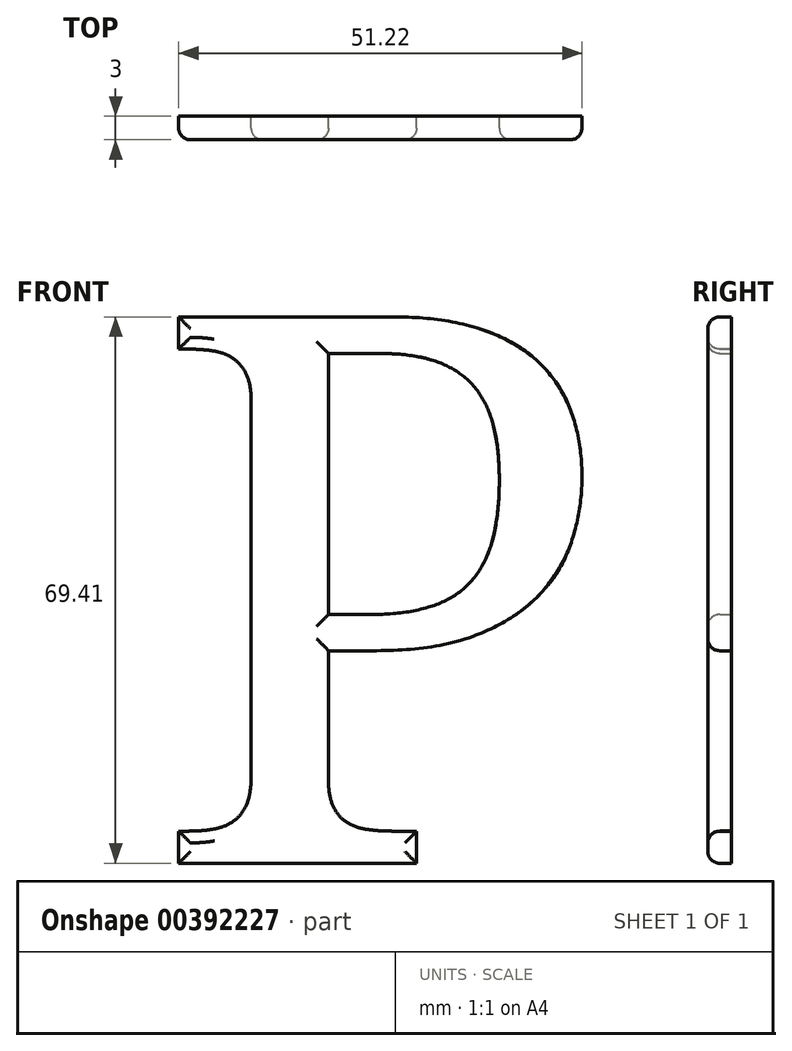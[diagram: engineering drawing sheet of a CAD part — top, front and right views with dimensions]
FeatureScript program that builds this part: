
annotation { "Feature Type Name" : "Feature", "Feature Type Description" : "" }
export const myFeature = defineFeature(function(context is Context, id is Id, definition is map)
    precondition{}
    {
        {
            var Q0;
            Q0=qCreatedBy(makeId("Front.planeOp"),FACE);
            var sketch = newSketch(context, id + "F0", { "sketchPlane" : qUnion([Q0])});
            skText(sketch, "E0", { "text": "P", "fontName": "NotoSerif-Regular.ttf"});
            const initialGuessF0  = {"E0": [0, 0, 1, 0, 0.07]};
            skSetInitialGuess(sketch, initialGuessF0);
            skSolve(sketch);
        }
        {
            var Q0;
            Q0 = qSketchRegion(id + "F0", true);
            extrude(context, id + "F1", {"entities" : qUnion([Q0]), "depth" : 3 * mm});
        }
        {
            var Q0;
            Q0=makeQuery(id+"F1.opExtrude","CAP_FACE",FACE,{"disambiguationData":[OSD([sQuery(id+"F0.wireOp",EDGE,"E0.sketch_text.stroke-0"),sQuery(id+"F0.wireOp",EDGE,"E0.sketch_text.stroke-1"),sQuery(id+"F0.wireOp",EDGE,"E0.sketch_text.stroke-2"),sQuery(id+"F0.wireOp",EDGE,"E0.sketch_text.stroke-3"),sQuery(id+"F0.wireOp",EDGE,"E0.sketch_text.stroke-4"),sQuery(id+"F0.wireOp",EDGE,"E0.sketch_text.stroke-5"),sQuery(id+"F0.wireOp",EDGE,"E0.sketch_text.stroke-6"),sQuery(id+"F0.wireOp",EDGE,"E0.sketch_text.stroke-7"),sQuery(id+"F0.wireOp",EDGE,"E0.sketch_text.stroke-8"),sQuery(id+"F0.wireOp",EDGE,"E0.sketch_text.stroke-9"),sQuery(id+"F0.wireOp",EDGE,"E0.sketch_text.stroke-10"),sQuery(id+"F0.wireOp",EDGE,"E0.sketch_text.stroke-11"),sQuery(id+"F0.wireOp",EDGE,"E0.sketch_text.stroke-12"),sQuery(id+"F0.wireOp",EDGE,"E0.sketch_text.stroke-13"),sQuery(id+"F0.wireOp",EDGE,"E0.sketch_text.stroke-14"),sQuery(id+"F0.wireOp",EDGE,"E0.sketch_text.stroke-15"),sQuery(id+"F0.wireOp",EDGE,"E0.sketch_text.stroke-16"),sQuery(id+"F0.wireOp",EDGE,"E0.sketch_text.stroke-17"),sQuery(id+"F0.wireOp",EDGE,"E0.sketch_text.stroke-18"),sQuery(id+"F0.wireOp",EDGE,"E0.sketch_text.stroke-19"),sQuery(id+"F0.wireOp",EDGE,"E0.sketch_text.stroke-20"),sQuery(id+"F0.wireOp",EDGE,"E0.sketch_text.stroke-21"),sQuery(id+"F0.wireOp",EDGE,"E0.sketch_text.stroke-22"),sQuery(id+"F0.wireOp",EDGE,"E0.sketch_text.stroke-23"),sQuery(id+"F0.wireOp",EDGE,"E0.sketch_text.stroke-24"),sQuery(id+"F0.wireOp",EDGE,"E0.sketch_text.stroke-25"),sQuery(id+"F0.wireOp",EDGE,"E0.sketch_text.stroke-26"),sQuery(id+"F0.wireOp",EDGE,"E0.sketch_text.stroke-27"),sQuery(id+"F0.wireOp",EDGE,"E0.sketch_text.stroke-28"),sQuery(id+"F0.wireOp",EDGE,"E0.sketch_text.stroke-29"),sQuery(id+"F0.wireOp",EDGE,"E0.sketch_text.stroke-30"),sQuery(id+"F0.wireOp",EDGE,"E0.sketch_text.stroke-31"),sQuery(id+"F0.wireOp",EDGE,"E0.sketch_text.stroke-32"),sQuery(id+"F0.wireOp",EDGE,"E0.sketch_text.stroke-33"),sQuery(id+"F0.wireOp",EDGE,"E0.sketch_text.stroke-34"),sQuery(id+"F0.wireOp",EDGE,"E0.sketch_text.stroke-35"),sQuery(id+"F0.wireOp",EDGE,"E0.sketch_text.stroke-36"),sQuery(id+"F0.wireOp",EDGE,"E0.sketch_text.stroke-37"),sQuery(id+"F0.wireOp",EDGE,"E0.sketch_text.stroke-38"),sQuery(id+"F0.wireOp",EDGE,"E0.sketch_text.stroke-39"),sQuery(id+"F0.wireOp",EDGE,"E0.sketch_text.stroke-40"),sQuery(id+"F0.wireOp",EDGE,"E0.sketch_text.stroke-41")])],"isStart":false});
            fillet(context, id + "F2", {"entities" : qUnion([Q0]), "radius" : 1.5 * mm, "tangentPropagation" : true, "allowEdgeOverflow" : false});
        }
    });
